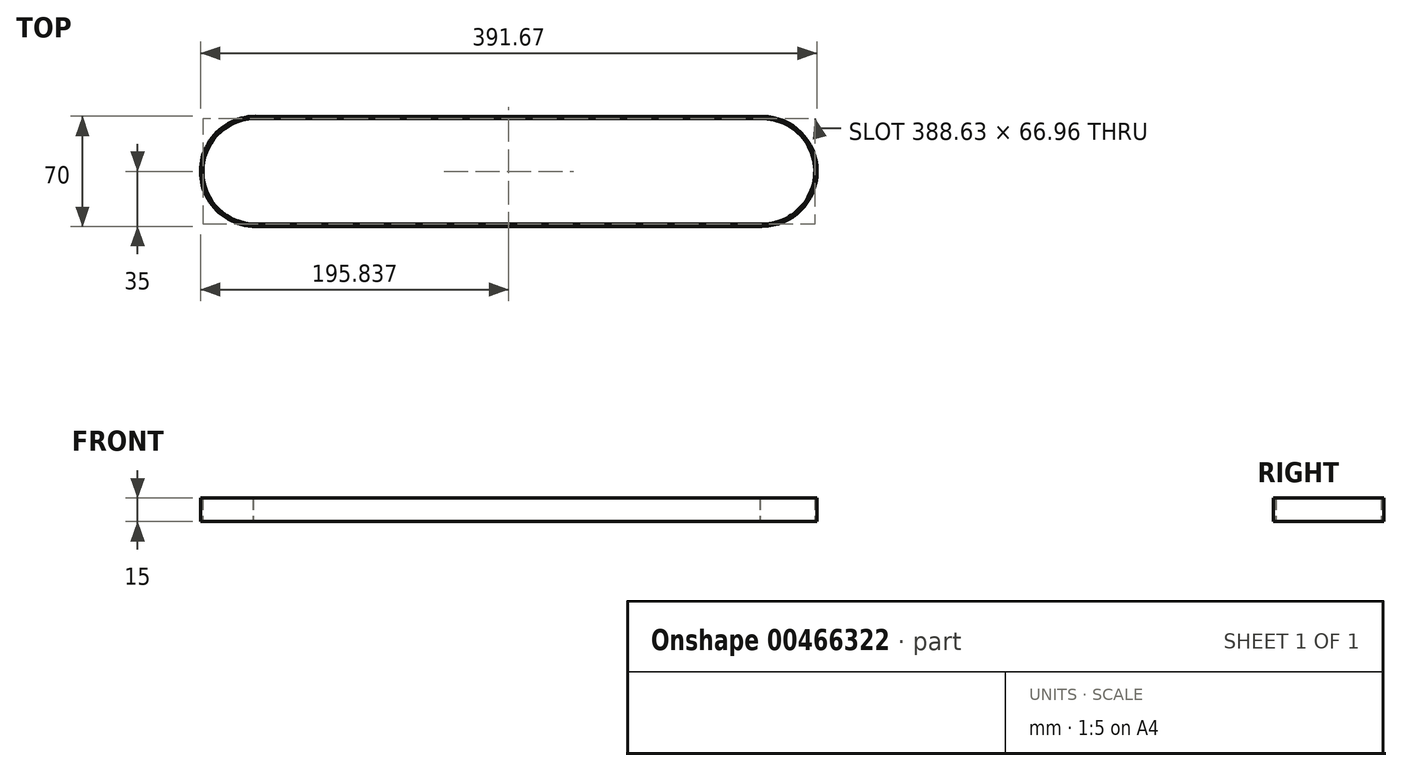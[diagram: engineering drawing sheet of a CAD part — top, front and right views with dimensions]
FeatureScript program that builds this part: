
annotation { "Feature Type Name" : "Feature", "Feature Type Description" : "" }
export const myFeature = defineFeature(function(context is Context, id is Id, definition is map)
    precondition{}
    {
        {
            var Q0;
            Q0=qCreatedBy(makeId("Top.planeOp"),FACE);
            var sketch = newSketch(context, id + "F0", { "sketchPlane" : qUnion([Q0])});
            skLineSegment(sketch, "E0", {"start": v(-154.77, 33.48) * mm, "end": v(166.96, 33.4) * mm});
            skLineSegment(sketch, "E1", {"start": v(-153.27, -33.48) * mm, "end": v(168.45, -33.4) * mm});
            skArc(sketch, "E2", {"start": v(-153.27, 35) * mm, "mid": v(-188.29, 0) * mm, "end": v(-153.27, -35) * mm});
            skArc(sketch, "E3", {"start": v(168.45, -34.93) * mm, "mid": v(203.38, 0) * mm, "end": v(168.45, 34.93) * mm});
            skLineSegment(sketch, "E4", {"start": v(168.45, 34.93) * mm, "end": v(-153.27, 35) * mm});
            skLineSegment(sketch, "E5", {"start": v(-153.27, -35) * mm, "end": v(168.45, -34.93) * mm});
            skArc(sketch, "E6", {"start": v(-154.77, 33.48) * mm, "mid": v(-186.77, -0.73) * mm, "end": v(-153.27, -33.48) * mm});
            skArc(sketch, "E7", {"start": v(168.45, -33.4) * mm, "mid": v(201.86, 0.77) * mm, "end": v(166.96, 33.4) * mm});
            skLineSegment(sketch, "E8", {"start": v(-153.28, 0) * mm, "end": v(168.45, 0) * mm});
            skLineSegment(sketch, "E9", {"start": v(168.45, 0) * mm, "end": v(168.45, 0) * mm});
            skSolve(sketch);
        }
        {
            var Q0;
            {var subQ1=sQuery(id+"F0.wireOp",EDGE,"E0");Q0=makeQuery(id+"F0.imprint","IMPRINT",FACE,{"disambiguationData":[TD([[makeQuery(id+"F0.imprint","IMPRINT",EDGE,{"derivedFrom":subQ1}),1.0]])]});}
            extrude(context, id + "F1", {"entities" : qUnion([Q0]), "depth" : 15 * mm});
        }
    });
